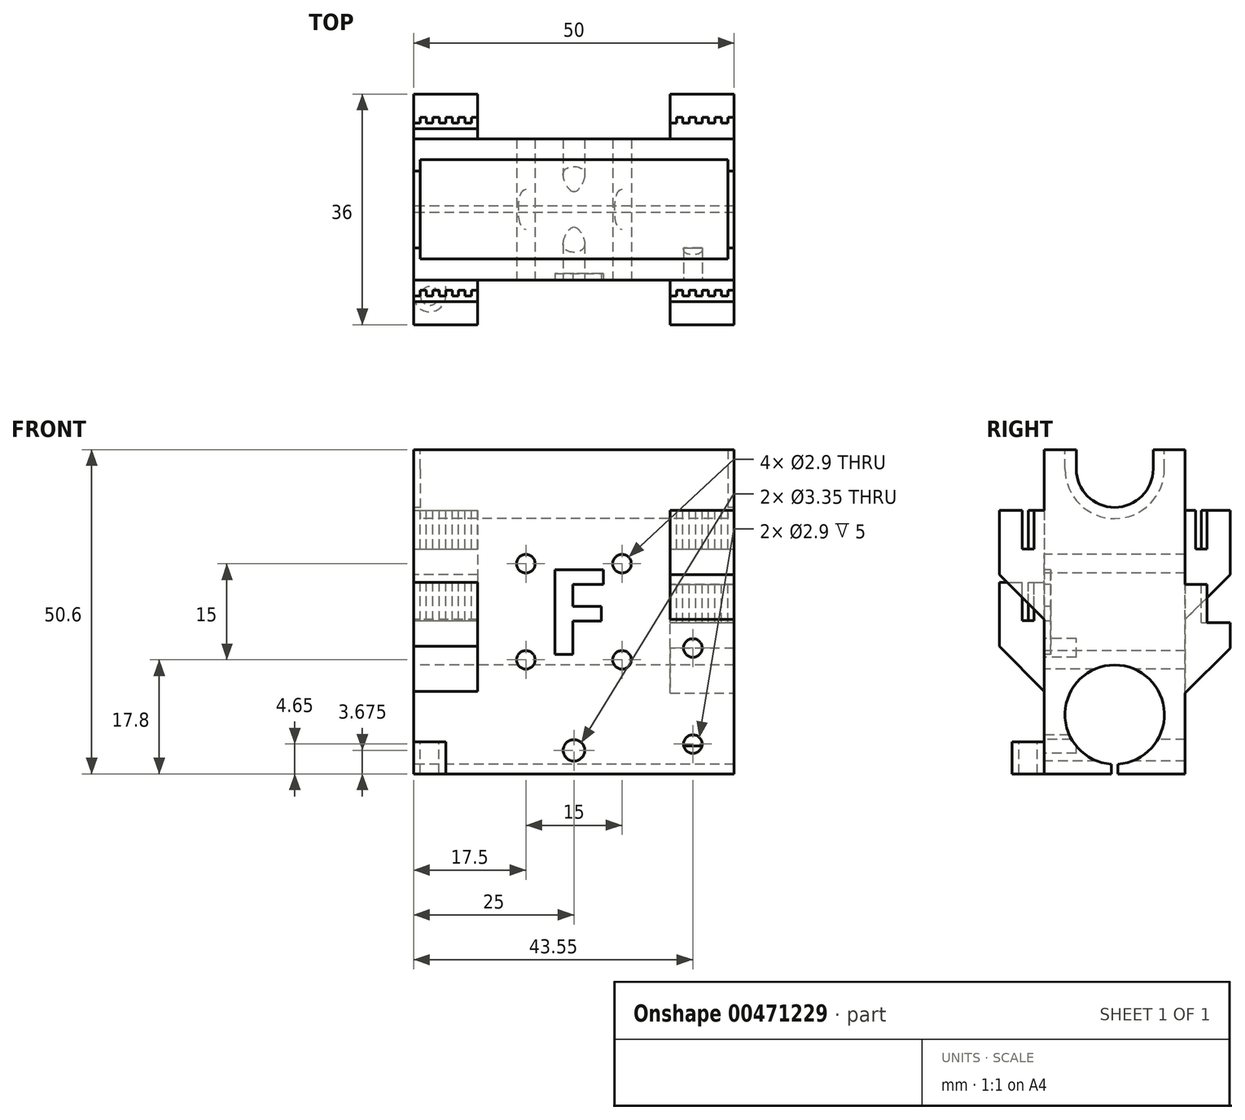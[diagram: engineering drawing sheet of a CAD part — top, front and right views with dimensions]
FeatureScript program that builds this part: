
annotation { "Feature Type Name" : "Feature", "Feature Type Description" : "" }
export const myFeature = defineFeature(function(context is Context, id is Id, definition is map)
    precondition{}
    {
        {
            assignVariable(context, id + "F0", {"name" : "LM8LUU", "anyValue" : 0});
        }
        {
            var Q0;
            Q0=qCreatedBy(makeId("Top.planeOp"),FACE);
            var sketch = newSketch(context, id + "F1", { "sketchPlane" : qUnion([Q0])});
            skLineSegment(sketch, "E0.bottom", {"start": v(0, 0) * mm, "end": v(50, 0) * mm});
            skLineSegment(sketch, "E0.top", {"start": v(0, 22) * mm, "end": v(50, 22) * mm});
            skLineSegment(sketch, "E0.left", {"start": v(0, 0) * mm, "end": v(0, 22) * mm});
            skLineSegment(sketch, "E0.right", {"start": v(50, 0) * mm, "end": v(50, 22) * mm});
            skSolve(sketch);
        }
        {
            var Q0;
            Q0=qSketchRegion(id+"F1",true);
            extrude(context, id + "F2", {"entities" : qUnion([Q0]), "depth" : 50.6 * mm});
        }
        {
            var Q0;
            Q0=makeQuery(id+"F2.opExtrude","SWEPT_FACE",FACE,{"disambiguationData":[OSD([sQuery(id+"F1.wireOp",EDGE,"E0.left")])]});
            var sketch = newSketch(context, id + "F3", { "sketchPlane" : qUnion([Q0])});
            skCircle(sketch, "E1", {"center": v(-11, 9.25) * mm, "radius": 7.75 * mm});
            skCircle(sketch, "E2", {"center": v(-11, 47.6) * mm, "radius": 6 * mm});
            skLineSegment(sketch, "E3", {"start": v(-22, 47.6) * mm, "end": v(0, 47.6) * mm, "construction": true});
            skLineSegment(sketch, "E4", {"start": v(-17, 50.6) * mm, "end": v(-17, 47.6) * mm});
            skLineSegment(sketch, "E5", {"start": v(-5, 50.6) * mm, "end": v(-5, 47.6) * mm});
            skLineSegment(sketch, "E6", {"start": v(-22, 9.25) * mm, "end": v(0, 9.25) * mm, "construction": true});
            skLineSegment(sketch, "E7", {"start": v(-11, 9.25) * mm, "end": v(-11, 0) * mm, "construction": true});
            skLineSegment(sketch, "E8", {"start": v(-11, 0) * mm, "end": v(-11.5, 0) * mm});
            skLineSegment(sketch, "E9", {"start": v(-11.5, 0) * mm, "end": v(-11.5, 1.52) * mm});
            skLineSegment(sketch, "E10", {"start": v(-11.5, 1.52) * mm, "end": v(-10.5, 1.52) * mm});
            skLineSegment(sketch, "E11", {"start": v(-10.5, 1.52) * mm, "end": v(-10.5, 0) * mm});
            skLineSegment(sketch, "E12", {"start": v(-10.5, 0) * mm, "end": v(-11, 0) * mm});
            skLineSegment(sketch, "E13", {"start": v(-11, 15.6) * mm, "end": v(-11, 17) * mm});
            skLineSegment(sketch, "E14", {"start": v(-11, 15.6) * mm, "end": v(-6.4, 15.5) * mm});
            skLineSegment(sketch, "E15", {"start": v(-11, 15.6) * mm, "end": v(-15.6, 15.5) * mm});
            skCircle(sketch, "E16", {"center": v(-11, 47.6) * mm, "radius": 7.75 * mm});
            skLineSegment(sketch, "E17", {"start": v(-3.25, 47.6) * mm, "end": v(-3.25, 50.6) * mm});
            skLineSegment(sketch, "E18", {"start": v(-18.75, 47.6) * mm, "end": v(-18.75, 50.6) * mm});
            skSolve(sketch);
        }
        {
            var Q0;
            {var subQ0=sQuery(id+"F3.wireOp",EDGE,"E14");var subQ1=sQuery(id+"F3.wireOp",EDGE,"E1");var subQ3=makeQuery(id+"F3.imprint","INTERSECT",VERTEX,{"disambiguationData":[OD(0.0)],"derivedFrom":[subQ1,subQ0]});Q0=makeQuery(id+"F3.imprint","IMPRINT",FACE,{"disambiguationData":[TD([[makeQuery(id+"F3.imprint","IMPRINT",EDGE,{"disambiguationData":[TD([[subQ3,-1.0]])],"derivedFrom":subQ1}),1.0]])]});}
            var Q1;
            {var subQ0=sQuery(id+"F3.wireOp",EDGE,"E15");var subQ1=sQuery(id+"F3.wireOp",EDGE,"E1");var subQ3=makeQuery(id+"F3.imprint","INTERSECT",VERTEX,{"disambiguationData":[OD(0.0)],"derivedFrom":[subQ1,subQ0]});Q1=makeQuery(id+"F3.imprint","IMPRINT",FACE,{"disambiguationData":[TD([[makeQuery(id+"F3.imprint","IMPRINT",EDGE,{"disambiguationData":[TD([[subQ3,1.0]])],"derivedFrom":subQ1}),1.0]])]});}
            var Q2;
            Q2=makeQuery(id+"F3.imprint","IMPRINT",FACE,{"disambiguationData":[TD([[makeQuery(id+"F3.imprint","IMPRINT",EDGE,{"derivedFrom":sQuery(id+"F3.wireOp",EDGE,"E8")}),-1.0]])]});
            var Q3;
            {var subQ0=sQuery(id+"F3.wireOp",EDGE,"E10");Q3=makeQuery(id+"F3.imprint","IMPRINT",FACE,{"disambiguationData":[TD([[makeQuery(id+"F3.imprint","IMPRINT",EDGE,{"derivedFrom":subQ0}),-1.0]])]});}
            var Q4;
            {var subQ3=sQuery(id+"F3.wireOp",EDGE,"E13");Q4=makeQuery(id+"F3.imprint","IMPRINT",FACE,{"disambiguationData":[TD([[makeQuery(id+"F3.imprint","IMPRINT",EDGE,{"derivedFrom":subQ3}),-1.0]])]});}
            var Q5;
            {var subQ3=sQuery(id+"F3.wireOp",EDGE,"E13");Q5=makeQuery(id+"F3.imprint","IMPRINT",FACE,{"disambiguationData":[TD([[makeQuery(id+"F3.imprint","IMPRINT",EDGE,{"derivedFrom":subQ3}),1.0]])]});}
            var Q6;
            {var subQ7=sQuery(id+"F3.wireOp",EDGE,"E10");Q6=makeQuery(id+"F3.imprint","IMPRINT",FACE,{"disambiguationData":[TD([[makeQuery(id+"F3.imprint","IMPRINT",EDGE,{"derivedFrom":subQ7}),1.0]])]});}
            var Q7;
            {var subQ3=sQuery(id+"F3.wireOp",EDGE,"E5");Q7=makeQuery(id+"F3.imprint","IMPRINT",FACE,{"disambiguationData":[TD([[makeQuery(id+"F3.imprint","IMPRINT",EDGE,{"derivedFrom":subQ3}),-1.0]])]});}
            var Q8;
            {var subQ0=sQuery(id+"F3.wireOp",EDGE,"E4");Q8=makeQuery(id+"F3.imprint","IMPRINT",FACE,{"disambiguationData":[TD([[makeQuery(id+"F3.imprint","IMPRINT",EDGE,{"derivedFrom":subQ0}),1.0]])]});}
            var Q9;
            {var subQ0=sQuery(id+"F3.wireOp",EDGE,"E4");Q9=makeQuery(id+"F3.imprint","IMPRINT",FACE,{"disambiguationData":[TD([[makeQuery(id+"F3.imprint","IMPRINT",EDGE,{"derivedFrom":subQ0}),1.0]])]});}
            var Q10;
            {var subQ3=sQuery(id+"F3.wireOp",EDGE,"E5");Q10=makeQuery(id+"F3.imprint","IMPRINT",FACE,{"disambiguationData":[TD([[makeQuery(id+"F3.imprint","IMPRINT",EDGE,{"derivedFrom":subQ3}),-1.0]])]});}
            var Q11;
            {var subQ1=sQuery(id+"F3.wireOp",EDGE,"E2");var subQ4=makeQuery(id+"F3.imprint","INTERSECT",VERTEX,{"derivedFrom":[subQ1,sQuery(id+"F3.wireOp",EDGE,"E5")]});Q11=makeQuery(id+"F3.imprint","IMPRINT",FACE,{"disambiguationData":[TD([[makeQuery(id+"F3.imprint","IMPRINT",EDGE,{"disambiguationData":[TD([[subQ4,-1.0]])],"derivedFrom":subQ1}),1.0]])]});}
            extrude(context, id + "F4", {"entities" : qUnion([Q0, Q1, Q2, Q3, Q4, Q5, Q6, Q7, Q8, Q9, Q10, Q11]), "operationType" : NewBodyOperationType.REMOVE, "endBound" : BoundingType.THROUGH_ALL, "oppositeDirection" : true, "depth" : 25 * mm});
        }
        {
            var Q0;
            {var subQ3=sQuery(id+"F3.wireOp",EDGE,"E4");Q0=makeQuery(id+"F3.imprint","IMPRINT",FACE,{"disambiguationData":[TD([[makeQuery(id+"F3.imprint","IMPRINT",EDGE,{"derivedFrom":subQ3}),-1.0]])]});}
            var Q1;
            {var subQ3=sQuery(id+"F3.wireOp",EDGE,"E18");Q1=makeQuery(id+"F3.imprint","IMPRINT",FACE,{"disambiguationData":[TD([[makeQuery(id+"F3.imprint","IMPRINT",EDGE,{"derivedFrom":subQ3}),-1.0]])]});}
            var Q2;
            {var subQ3=sQuery(id+"F3.wireOp",EDGE,"E17");Q2=makeQuery(id+"F3.imprint","IMPRINT",FACE,{"disambiguationData":[TD([[makeQuery(id+"F3.imprint","IMPRINT",EDGE,{"derivedFrom":subQ3}),1.0]])]});}
            extrude(context, id + "F5", {"entities" : qUnion([Q0, Q1, Q2]), "operationType" : NewBodyOperationType.REMOVE, "oppositeDirection" : true, "depth" : 49 * mm});
        }
        {
            var Q0;
            {var subQ3=sQuery(id+"F3.wireOp",EDGE,"E4");Q0=makeQuery(id+"F3.imprint","IMPRINT",FACE,{"disambiguationData":[TD([[makeQuery(id+"F3.imprint","IMPRINT",EDGE,{"derivedFrom":subQ3}),-1.0]])]});}
            var Q1;
            {var subQ3=sQuery(id+"F3.wireOp",EDGE,"E18");Q1=makeQuery(id+"F3.imprint","IMPRINT",FACE,{"disambiguationData":[TD([[makeQuery(id+"F3.imprint","IMPRINT",EDGE,{"derivedFrom":subQ3}),-1.0]])]});}
            var Q2;
            {var subQ3=sQuery(id+"F3.wireOp",EDGE,"E17");Q2=makeQuery(id+"F3.imprint","IMPRINT",FACE,{"disambiguationData":[TD([[makeQuery(id+"F3.imprint","IMPRINT",EDGE,{"derivedFrom":subQ3}),1.0]])]});}
            extrude(context, id + "F6", {"entities" : qUnion([Q0, Q1, Q2]), "operationType" : NewBodyOperationType.ADD, "oppositeDirection" : true, "depth" : (25 - getVariable(context, 'LM8LUU')) * mm});
        }
        {
            var Q0;
            {var subQ3=sQuery(id+"F3.wireOp",EDGE,"E4");Q0=makeQuery(id+"F3.imprint","IMPRINT",FACE,{"disambiguationData":[TD([[makeQuery(id+"F3.imprint","IMPRINT",EDGE,{"derivedFrom":subQ3}),-1.0]])]});}
            var Q1;
            {var subQ3=sQuery(id+"F3.wireOp",EDGE,"E18");Q1=makeQuery(id+"F3.imprint","IMPRINT",FACE,{"disambiguationData":[TD([[makeQuery(id+"F3.imprint","IMPRINT",EDGE,{"derivedFrom":subQ3}),-1.0]])]});}
            var Q2;
            {var subQ3=sQuery(id+"F3.wireOp",EDGE,"E17");Q2=makeQuery(id+"F3.imprint","IMPRINT",FACE,{"disambiguationData":[TD([[makeQuery(id+"F3.imprint","IMPRINT",EDGE,{"derivedFrom":subQ3}),1.0]])]});}
            extrude(context, id + "F7", {"entities" : qUnion([Q0, Q1, Q2]), "operationType" : NewBodyOperationType.REMOVE, "oppositeDirection" : true, "depth" : (25 + getVariable(context, 'LM8LUU')) * mm});
        }
        {
            var Q0;
            {var subQ3=sQuery(id+"F3.wireOp",EDGE,"E4");Q0=makeQuery(id+"F3.imprint","IMPRINT",FACE,{"disambiguationData":[TD([[makeQuery(id+"F3.imprint","IMPRINT",EDGE,{"derivedFrom":subQ3}),-1.0]])]});}
            var Q1;
            {var subQ3=sQuery(id+"F3.wireOp",EDGE,"E18");Q1=makeQuery(id+"F3.imprint","IMPRINT",FACE,{"disambiguationData":[TD([[makeQuery(id+"F3.imprint","IMPRINT",EDGE,{"derivedFrom":subQ3}),-1.0]])]});}
            var Q2;
            {var subQ3=sQuery(id+"F3.wireOp",EDGE,"E17");Q2=makeQuery(id+"F3.imprint","IMPRINT",FACE,{"disambiguationData":[TD([[makeQuery(id+"F3.imprint","IMPRINT",EDGE,{"derivedFrom":subQ3}),1.0]])]});}
            extrude(context, id + "F8", {"entities" : qUnion([Q0, Q1, Q2]), "operationType" : NewBodyOperationType.ADD, "oppositeDirection" : true, "depth" : 1 * mm});
        }
        {
            var Q0;
            Q0=makeQuery(id+"F2.opExtrude","SWEPT_FACE",FACE,{"disambiguationData":[OSD([sQuery(id+"F1.wireOp",EDGE,"E0.bottom")])]});
            var sketch = newSketch(context, id + "F9", { "sketchPlane" : qUnion([Q0])});
            skLineSegment(sketch, "E19.bottom", {"start": v(0, 29.9) * mm, "end": v(10, 29.9) * mm});
            skLineSegment(sketch, "E19.top", {"start": v(0, 9.9) * mm, "end": v(10, 9.9) * mm});
            skLineSegment(sketch, "E19.left", {"start": v(0, 29.9) * mm, "end": v(0, 9.9) * mm});
            skLineSegment(sketch, "E19.right", {"start": v(10, 29.9) * mm, "end": v(10, 9.9) * mm});
            skLineSegment(sketch, "E20.bottom", {"start": v(50, 41.1) * mm, "end": v(40, 41.1) * mm});
            skLineSegment(sketch, "E20.top", {"start": v(50, 21.1) * mm, "end": v(40, 21.1) * mm});
            skLineSegment(sketch, "E20.left", {"start": v(50, 41.1) * mm, "end": v(50, 21.1) * mm});
            skLineSegment(sketch, "E20.right", {"start": v(40, 41.1) * mm, "end": v(40, 21.1) * mm});
            skPoint(sketch, "E21", {"position": v(0, 47.6) * mm});
            skPoint(sketch, "E22", {"position": v(0, 9.4) * mm});
            skSolve(sketch);
        }
        {
            var Q0;
            Q0=qSketchRegion(id+"F9",true);
            extrude(context, id + "F10", {"entities" : qUnion([Q0]), "operationType" : NewBodyOperationType.ADD, "depth" : 7 * mm});
        }
        {
            var Q0;
            Q0=makeQuery(id+"F10.opExtrude","CAP_EDGE",EDGE,{"disambiguationData":[OSD([sQuery(id+"F9.wireOp",EDGE,"E19.top")])],"isStart":false});
            var Q1;
            Q1=makeQuery(id+"F10.opExtrude","CAP_EDGE",EDGE,{"disambiguationData":[OSD([sQuery(id+"F9.wireOp",EDGE,"E20.top")])],"isStart":false});
            chamfer(context, id + "F11", {"entities" : qUnion([Q0, Q1]), "width" : 10 * mm, "tangentPropagation" : true});
        }
        {
            var Q0;
            Q0=makeQuery(id+"F10.opExtrude","SWEPT_FACE",FACE,{"disambiguationData":[OSD([sQuery(id+"F9.wireOp",EDGE,"E19.bottom")])]});
            var sketch = newSketch(context, id + "F12", { "sketchPlane" : qUnion([Q0])});
            skLineSegment(sketch, "E23", {"start": v(-935.9, 0) * mm, "end": v(-935.88, -4.54) * mm});
            skLineSegment(sketch, "E24.left", {"start": v(0, -3.4) * mm, "end": v(0, -1.6) * mm});
            skLineSegment(sketch, "E25", {"start": v(6, -2.5) * mm, "end": v(7, -2.5) * mm});
            skLineSegment(sketch, "E26", {"start": v(4, -2.5) * mm, "end": v(5, -2.5) * mm});
            skLineSegment(sketch, "E27", {"start": v(0, -2.5) * mm, "end": v(1, -2.5) * mm});
            skLineSegment(sketch, "E28", {"start": v(7, -1.6) * mm, "end": v(8, -1.6) * mm});
            skLineSegment(sketch, "E29", {"start": v(2, -2.5) * mm, "end": v(3, -2.5) * mm});
            skLineSegment(sketch, "E30", {"start": v(3, -1.6) * mm, "end": v(4, -1.6) * mm});
            skLineSegment(sketch, "E31", {"start": v(8, -2.5) * mm, "end": v(9, -2.5) * mm});
            skLineSegment(sketch, "E32", {"start": v(8, -1.6) * mm, "end": v(8, -2.5) * mm});
            skLineSegment(sketch, "E33", {"start": v(9, -2.5) * mm, "end": v(9, -1.6) * mm});
            skLineSegment(sketch, "E34", {"start": v(10, -1.6) * mm, "end": v(10, -2.5) * mm});
            skLineSegment(sketch, "E35", {"start": v(6, -1.6) * mm, "end": v(6, -2.5) * mm});
            skLineSegment(sketch, "E36", {"start": v(2, -1.6) * mm, "end": v(2, -2.5) * mm});
            skLineSegment(sketch, "E37", {"start": v(1, -1.6) * mm, "end": v(2, -1.6) * mm});
            skLineSegment(sketch, "E38", {"start": v(1, -2.5) * mm, "end": v(1, -1.6) * mm});
            skLineSegment(sketch, "E39", {"start": v(9, -1.6) * mm, "end": v(10, -1.6) * mm});
            skLineSegment(sketch, "E40", {"start": v(5, -1.6) * mm, "end": v(6, -1.6) * mm});
            skLineSegment(sketch, "E41", {"start": v(5, -2.5) * mm, "end": v(5, -1.6) * mm});
            skLineSegment(sketch, "E42", {"start": v(3, -2.5) * mm, "end": v(3, -1.6) * mm});
            skLineSegment(sketch, "E43", {"start": v(4, -1.6) * mm, "end": v(4, -2.5) * mm});
            skLineSegment(sketch, "E44", {"start": v(7, -2.5) * mm, "end": v(7, -1.6) * mm});
            skLineSegment(sketch, "E45", {"start": v(0, -1.6) * mm, "end": v(0, -2.5) * mm});
            skLineSegment(sketch, "E46", {"start": v(10, -2.5) * mm, "end": v(10, -3.4) * mm});
            skLineSegment(sketch, "E47", {"start": v(0, -3.4) * mm, "end": v(10, -3.4) * mm});
            skLineSegment(sketch, "E48", {"start": v(5.3, -1.6) * mm, "end": v(5.3, 0) * mm});
            skSolve(sketch);
        }
        {
            var Q0;
            Q0=qSketchRegion(id+"F12",true);
            extrude(context, id + "F13", {"entities" : qUnion([Q0]), "operationType" : NewBodyOperationType.REMOVE, "oppositeDirection" : true, "depth" : 6 * mm});
        }
        {
            var Q0;
            Q0=makeQuery(id+"F10.opExtrude","SWEPT_FACE",FACE,{"disambiguationData":[OSD([sQuery(id+"F9.wireOp",EDGE,"E20.bottom")])]});
            var sketch = newSketch(context, id + "F14", { "sketchPlane" : qUnion([Q0])});
            skLineSegment(sketch, "E49.left", {"start": v(40, -3.4) * mm, "end": v(40, -1.6) * mm});
            skLineSegment(sketch, "E50", {"start": v(46, -2.5) * mm, "end": v(47, -2.5) * mm});
            skLineSegment(sketch, "E51", {"start": v(44, -2.5) * mm, "end": v(45, -2.5) * mm});
            skLineSegment(sketch, "E52", {"start": v(40, -2.5) * mm, "end": v(41, -2.5) * mm});
            skLineSegment(sketch, "E53", {"start": v(47, -1.6) * mm, "end": v(48, -1.6) * mm});
            skLineSegment(sketch, "E54", {"start": v(42, -2.5) * mm, "end": v(43, -2.5) * mm});
            skLineSegment(sketch, "E55", {"start": v(43, -1.6) * mm, "end": v(44, -1.6) * mm});
            skLineSegment(sketch, "E56", {"start": v(48, -2.5) * mm, "end": v(49, -2.5) * mm});
            skLineSegment(sketch, "E57", {"start": v(48, -1.6) * mm, "end": v(48, -2.5) * mm});
            skLineSegment(sketch, "E58", {"start": v(49, -2.5) * mm, "end": v(49, -1.6) * mm});
            skLineSegment(sketch, "E59", {"start": v(50, -1.6) * mm, "end": v(50, -2.5) * mm});
            skLineSegment(sketch, "E60", {"start": v(46, -1.6) * mm, "end": v(46, -2.5) * mm});
            skLineSegment(sketch, "E61", {"start": v(42, -1.6) * mm, "end": v(42, -2.5) * mm});
            skLineSegment(sketch, "E62", {"start": v(41, -1.6) * mm, "end": v(42, -1.6) * mm});
            skLineSegment(sketch, "E63", {"start": v(41, -2.5) * mm, "end": v(41, -1.6) * mm});
            skLineSegment(sketch, "E64", {"start": v(49, -1.6) * mm, "end": v(50, -1.6) * mm});
            skLineSegment(sketch, "E65", {"start": v(45, -1.6) * mm, "end": v(46, -1.6) * mm});
            skLineSegment(sketch, "E66", {"start": v(45, -2.5) * mm, "end": v(45, -1.6) * mm});
            skLineSegment(sketch, "E67", {"start": v(43, -2.5) * mm, "end": v(43, -1.6) * mm});
            skLineSegment(sketch, "E68", {"start": v(44, -1.6) * mm, "end": v(44, -2.5) * mm});
            skLineSegment(sketch, "E69", {"start": v(47, -2.5) * mm, "end": v(47, -1.6) * mm});
            skLineSegment(sketch, "E70", {"start": v(40, -1.6) * mm, "end": v(40, -2.5) * mm});
            skLineSegment(sketch, "E71", {"start": v(50, -2.5) * mm, "end": v(50, -3.4) * mm});
            skLineSegment(sketch, "E72", {"start": v(40, -3.4) * mm, "end": v(50, -3.4) * mm});
            skLineSegment(sketch, "E73", {"start": v(45.23, -1.6) * mm, "end": v(45.23, 0) * mm});
            skSolve(sketch);
        }
        {
            var Q0;
            Q0=qSketchRegion(id+"F14",true);
            extrude(context, id + "F15", {"entities" : qUnion([Q0]), "operationType" : NewBodyOperationType.REMOVE, "oppositeDirection" : true, "depth" : 6 * mm});
        }
        {
            var Q0;
            Q0=makeQuery(id+"F2.opExtrude","SWEPT_FACE",FACE,{"disambiguationData":[OSD([sQuery(id+"F1.wireOp",EDGE,"E0.top")])]});
            var sketch = newSketch(context, id + "F16", { "sketchPlane" : qUnion([Q0])});
            skLineSegment(sketch, "E74.bottom", {"start": v(-50, 9.6) * mm, "end": v(-40, 9.6) * mm});
            skLineSegment(sketch, "E74.top", {"start": v(-50, 29.6) * mm, "end": v(-40, 29.6) * mm});
            skLineSegment(sketch, "E74.left", {"start": v(-50, 9.6) * mm, "end": v(-50, 29.6) * mm});
            skLineSegment(sketch, "E74.right", {"start": v(-40, 9.6) * mm, "end": v(-40, 29.6) * mm});
            skLineSegment(sketch, "E75.bottom", {"start": v(0, 41.1) * mm, "end": v(-10, 41.1) * mm});
            skLineSegment(sketch, "E75.top", {"start": v(0, 21.1) * mm, "end": v(-10, 21.1) * mm});
            skLineSegment(sketch, "E75.left", {"start": v(0, 41.1) * mm, "end": v(0, 21.1) * mm});
            skLineSegment(sketch, "E75.right", {"start": v(-10, 41.1) * mm, "end": v(-10, 21.1) * mm});
            skSolve(sketch);
        }
        {
            var Q0;
            Q0=qSketchRegion(id+"F16",true);
            extrude(context, id + "F17", {"entities" : qUnion([Q0]), "operationType" : NewBodyOperationType.ADD, "depth" : 7 * mm});
        }
        {
            var Q0;
            Q0=makeQuery(id+"F17.opExtrude","SWEPT_FACE",FACE,{"disambiguationData":[OSD([sQuery(id+"F16.wireOp",EDGE,"E74.top")])]});
            var sketch = newSketch(context, id + "F18", { "sketchPlane" : qUnion([Q0])});
            skLineSegment(sketch, "E76.left", {"start": v(40, 23.6) * mm, "end": v(40, 25.4) * mm});
            skLineSegment(sketch, "E77", {"start": v(46, 24.5) * mm, "end": v(47, 24.5) * mm});
            skLineSegment(sketch, "E78", {"start": v(44, 24.5) * mm, "end": v(45, 24.5) * mm});
            skLineSegment(sketch, "E79", {"start": v(40, 24.5) * mm, "end": v(41, 24.5) * mm});
            skLineSegment(sketch, "E80", {"start": v(47, 25.4) * mm, "end": v(48, 25.4) * mm});
            skLineSegment(sketch, "E81", {"start": v(42, 24.5) * mm, "end": v(43, 24.5) * mm});
            skLineSegment(sketch, "E82", {"start": v(43, 25.4) * mm, "end": v(44, 25.4) * mm});
            skLineSegment(sketch, "E83", {"start": v(48, 24.5) * mm, "end": v(49, 24.5) * mm});
            skLineSegment(sketch, "E84", {"start": v(48, 25.4) * mm, "end": v(48, 24.5) * mm});
            skLineSegment(sketch, "E85", {"start": v(49, 24.5) * mm, "end": v(49, 25.4) * mm});
            skLineSegment(sketch, "E86", {"start": v(50, 25.4) * mm, "end": v(50, 24.5) * mm});
            skLineSegment(sketch, "E87", {"start": v(46, 25.4) * mm, "end": v(46, 24.5) * mm});
            skLineSegment(sketch, "E88", {"start": v(42, 25.4) * mm, "end": v(42, 24.5) * mm});
            skLineSegment(sketch, "E89", {"start": v(41, 25.4) * mm, "end": v(42, 25.4) * mm});
            skLineSegment(sketch, "E90", {"start": v(41, 24.5) * mm, "end": v(41, 25.4) * mm});
            skLineSegment(sketch, "E91", {"start": v(49, 25.4) * mm, "end": v(50, 25.4) * mm});
            skLineSegment(sketch, "E92", {"start": v(45, 25.4) * mm, "end": v(46, 25.4) * mm});
            skLineSegment(sketch, "E93", {"start": v(45, 24.5) * mm, "end": v(45, 25.4) * mm});
            skLineSegment(sketch, "E94", {"start": v(43, 24.5) * mm, "end": v(43, 25.4) * mm});
            skLineSegment(sketch, "E95", {"start": v(44, 25.4) * mm, "end": v(44, 24.5) * mm});
            skLineSegment(sketch, "E96", {"start": v(47, 24.5) * mm, "end": v(47, 25.4) * mm});
            skLineSegment(sketch, "E97", {"start": v(40, 25.4) * mm, "end": v(40, 24.5) * mm});
            skLineSegment(sketch, "E98", {"start": v(50, 24.5) * mm, "end": v(50, 23.6) * mm});
            skLineSegment(sketch, "E99", {"start": v(40, 23.6) * mm, "end": v(50, 23.6) * mm});
            skLineSegment(sketch, "E100", {"start": v(45, 23.6) * mm, "end": v(45, 22) * mm});
            skSolve(sketch);
        }
        {
            var Q0;
            {var subQ4=sQuery(id+"F18.wireOp",EDGE,"E76.left");Q0=makeQuery(id+"F18.imprint","IMPRINT",FACE,{"disambiguationData":[TD([[makeQuery(id+"F18.imprint","IMPRINT",EDGE,{"derivedFrom":subQ4}),1.0]])]});}
            extrude(context, id + "F19", {"entities" : qUnion([Q0]), "operationType" : NewBodyOperationType.REMOVE, "oppositeDirection" : true, "depth" : 6 * mm});
        }
        {
            var Q0;
            Q0=makeQuery(id+"F17.opExtrude","SWEPT_FACE",FACE,{"disambiguationData":[OSD([sQuery(id+"F16.wireOp",EDGE,"E75.bottom")])]});
            var sketch = newSketch(context, id + "F20", { "sketchPlane" : qUnion([Q0])});
            skLineSegment(sketch, "E101", {"start": v(6, 24.5) * mm, "end": v(7, 24.5) * mm});
            skLineSegment(sketch, "E102", {"start": v(4, 24.5) * mm, "end": v(5, 24.5) * mm});
            skLineSegment(sketch, "E103", {"start": v(0, 24.5) * mm, "end": v(1, 24.5) * mm});
            skLineSegment(sketch, "E104", {"start": v(7, 25.4) * mm, "end": v(8, 25.4) * mm});
            skLineSegment(sketch, "E105", {"start": v(2, 24.5) * mm, "end": v(3, 24.5) * mm});
            skLineSegment(sketch, "E106", {"start": v(3, 25.4) * mm, "end": v(4, 25.4) * mm});
            skLineSegment(sketch, "E107", {"start": v(8, 24.5) * mm, "end": v(9, 24.5) * mm});
            skLineSegment(sketch, "E108", {"start": v(8, 25.4) * mm, "end": v(8, 24.5) * mm});
            skLineSegment(sketch, "E109", {"start": v(9, 24.5) * mm, "end": v(9, 25.4) * mm});
            skLineSegment(sketch, "E110", {"start": v(10, 25.4) * mm, "end": v(10, 24.5) * mm});
            skLineSegment(sketch, "E111", {"start": v(6, 25.4) * mm, "end": v(6, 24.5) * mm});
            skLineSegment(sketch, "E112", {"start": v(2, 25.4) * mm, "end": v(2, 24.5) * mm});
            skLineSegment(sketch, "E113", {"start": v(1, 25.4) * mm, "end": v(2, 25.4) * mm});
            skLineSegment(sketch, "E114", {"start": v(1, 24.5) * mm, "end": v(1, 25.4) * mm});
            skLineSegment(sketch, "E115", {"start": v(9, 25.4) * mm, "end": v(10, 25.4) * mm});
            skLineSegment(sketch, "E116", {"start": v(5, 25.4) * mm, "end": v(6, 25.4) * mm});
            skLineSegment(sketch, "E117", {"start": v(5, 24.5) * mm, "end": v(5, 25.4) * mm});
            skLineSegment(sketch, "E118", {"start": v(3, 24.5) * mm, "end": v(3, 25.4) * mm});
            skLineSegment(sketch, "E119", {"start": v(4, 25.4) * mm, "end": v(4, 24.5) * mm});
            skLineSegment(sketch, "E120", {"start": v(7, 24.5) * mm, "end": v(7, 25.4) * mm});
            skLineSegment(sketch, "E121", {"start": v(10, 24.5) * mm, "end": v(10, 23.6) * mm});
            skLineSegment(sketch, "E122", {"start": v(0, 23.6) * mm, "end": v(10, 23.6) * mm});
            skLineSegment(sketch, "E123", {"start": v(5, 23.6) * mm, "end": v(5, 22) * mm});
            skLineSegment(sketch, "E124", {"start": v(0, 23.6) * mm, "end": v(0, 24.5) * mm});
            skSolve(sketch);
        }
        {
            var Q0;
            Q0=makeQuery(id+"F20.imprint","IMPRINT",FACE,{"disambiguationData":[TD([[makeQuery(id+"F20.imprint","IMPRINT",EDGE,{"derivedFrom":sQuery(id+"F20.wireOp",EDGE,"E101")}),-1.0]])]});
            extrude(context, id + "F21", {"entities" : qUnion([Q0]), "operationType" : NewBodyOperationType.REMOVE, "oppositeDirection" : true, "depth" : 6 * mm});
        }
        {
            var Q0;
            Q0=makeQuery(id+"F17.opExtrude","CAP_EDGE",EDGE,{"disambiguationData":[OSD([sQuery(id+"F16.wireOp",EDGE,"E75.top")])],"isStart":false});
            var Q1;
            Q1=makeQuery(id+"F17.opExtrude","CAP_EDGE",EDGE,{"disambiguationData":[OSD([sQuery(id+"F16.wireOp",EDGE,"E74.bottom")])],"isStart":false});
            chamfer(context, id + "F22", {"entities" : qUnion([Q0, Q1]), "width" : 10 * mm, "tangentPropagation" : true});
        }
        {
            var Q0;
            Q0=makeQuery(id+"F2.opExtrude","SWEPT_FACE",FACE,{"disambiguationData":[OSD([sQuery(id+"F1.wireOp",EDGE,"E0.bottom")])]});
            var sketch = newSketch(context, id + "F23", { "sketchPlane" : qUnion([Q0])});
            skCircle(sketch, "E125", {"center": v(17.5, 32.8) * mm, "radius": 1.45 * mm});
            skCircle(sketch, "E126", {"center": v(32.5, 32.8) * mm, "radius": 1.45 * mm});
            skCircle(sketch, "E127", {"center": v(17.5, 17.8) * mm, "radius": 1.45 * mm});
            skCircle(sketch, "E128", {"center": v(32.5, 17.8) * mm, "radius": 1.45 * mm});
            skLineSegment(sketch, "E129", {"start": v(17.5, 32.8) * mm, "end": v(0, 32.8) * mm});
            skLineSegment(sketch, "E130", {"start": v(32.5, 17.8) * mm, "end": v(50, 17.8) * mm});
            skLineSegment(sketch, "E131", {"start": v(32.5, 32.8) * mm, "end": v(32.5, 50.6) * mm});
            skLineSegment(sketch, "E132", {"start": v(17.5, 17.8) * mm, "end": v(17.5, 0) * mm});
            skCircle(sketch, "E133", {"center": v(25, 3.68) * mm, "radius": 1.68 * mm});
            skLineSegment(sketch, "E134", {"start": v(25, 0) * mm, "end": v(25, 13.82) * mm, "construction": true});
            skSolve(sketch);
        }
        {
            var Q0;
            Q0=qSketchRegion(id+"F23",true);
            var Q1;
            Q1=makeQuery(id+"F23.imprint","IMPRINT",FACE,{"disambiguationData":[TD([[makeQuery(id+"F23.imprint","IMPRINT",EDGE,{"derivedFrom":sQuery(id+"F23.wireOp",EDGE,"E125")}),1.0]])]});
            var Q2;
            Q2=makeQuery(id+"F23.imprint","IMPRINT",FACE,{"disambiguationData":[TD([[makeQuery(id+"F23.imprint","IMPRINT",EDGE,{"derivedFrom":sQuery(id+"F23.wireOp",EDGE,"E126")}),1.0]])]});
            var Q3;
            Q3=makeQuery(id+"F23.imprint","IMPRINT",FACE,{"disambiguationData":[TD([[makeQuery(id+"F23.imprint","IMPRINT",EDGE,{"derivedFrom":sQuery(id+"F23.wireOp",EDGE,"E128")}),1.0]])]});
            var Q4;
            Q4=makeQuery(id+"F23.imprint","IMPRINT",FACE,{"disambiguationData":[TD([[makeQuery(id+"F23.imprint","IMPRINT",EDGE,{"derivedFrom":sQuery(id+"F23.wireOp",EDGE,"E127")}),1.0]])]});
            extrude(context, id + "F24", {"entities" : qUnion([Q0, Q1, Q2, Q3, Q4]), "operationType" : NewBodyOperationType.REMOVE, "endBound" : BoundingType.THROUGH_ALL, "oppositeDirection" : true, "depth" : 25 * mm});
        }
        {
            var Q0;
            Q0=makeQuery(id+"F2.opExtrude","SWEPT_FACE",FACE,{"disambiguationData":[OSD([sQuery(id+"F1.wireOp",EDGE,"E0.bottom")])]});
            var sketch = newSketch(context, id + "F25", { "sketchPlane" : qUnion([Q0])});
            skCircle(sketch, "E135", {"center": v(43.55, 19.65) * mm, "radius": 1.45 * mm});
            skCircle(sketch, "E136", {"center": v(43.55, 4.65) * mm, "radius": 1.45 * mm});
            skSolve(sketch);
        }
        {
            var Q0;
            Q0=qSketchRegion(id+"F25",true);
            extrude(context, id + "F26", {"entities" : qUnion([Q0]), "operationType" : NewBodyOperationType.REMOVE, "oppositeDirection" : true, "depth" : 5 * mm});
        }
        {
            var Q0;
            Q0=makeQuery(id+"F2.opExtrude","SWEPT_FACE",FACE,{"disambiguationData":[OSD([sQuery(id+"F1.wireOp",EDGE,"E0.bottom")])]});
            var sketch = newSketch(context, id + "F27", { "sketchPlane" : qUnion([Q0])});
            skText(sketch, "E137", { "text": "F", "fontName": "OpenSans-Bold.ttf"});
            skLineSegment(sketch, "E138", {"start": v(17.5, 32.8) * mm, "end": v(17.5, 17.8) * mm, "construction": true});
            skLineSegment(sketch, "E139", {"start": v(17.5, 17.8) * mm, "end": v(32.5, 17.8) * mm, "construction": true});
            skLineSegment(sketch, "E140", {"start": v(32.5, 17.8) * mm, "end": v(32.5, 32.8) * mm, "construction": true});
            skLineSegment(sketch, "E141", {"start": v(32.5, 32.8) * mm, "end": v(17.5, 32.8) * mm, "construction": true});
            skLineSegment(sketch, "E142", {"start": v(17.5, 25.3) * mm, "end": v(20.4, 25.3) * mm, "construction": true});
            skLineSegment(sketch, "E143", {"start": v(29.6, 25.3) * mm, "end": v(32.5, 25.3) * mm, "construction": true});
            skLineSegment(sketch, "E144", {"start": v(25, 18.66) * mm, "end": v(25, 17.8) * mm, "construction": true});
            skLineSegment(sketch, "E145", {"start": v(25, 32.8) * mm, "end": v(25, 31.94) * mm, "construction": true});
            const initialGuessF27  = {"E137": [0.0204, 0.01866, 1, 0, 0.01328]};
            skSetInitialGuess(sketch, initialGuessF27);
            skSolve(sketch);
        }
        {
            var Q0;
            Q0=qSketchRegion(id+"F27",true);
            extrude(context, id + "F28", {"entities" : qUnion([Q0]), "operationType" : NewBodyOperationType.REMOVE, "oppositeDirection" : true, "depth" : 1 * mm});
        }
        {
            var Q0;
            Q0=makeQuery(id+"F2.opExtrude","SWEPT_FACE",FACE,{"disambiguationData":[OSD([sQuery(id+"F1.wireOp",EDGE,"E0.bottom")])]});
            var sketch = newSketch(context, id + "F29", { "sketchPlane" : qUnion([Q0])});
            skLineSegment(sketch, "E146.bottom", {"start": v(0, 0) * mm, "end": v(5, 0) * mm});
            skLineSegment(sketch, "E146.top", {"start": v(0, 5) * mm, "end": v(5, 5) * mm});
            skLineSegment(sketch, "E146.left", {"start": v(0, 0) * mm, "end": v(0, 5) * mm});
            skLineSegment(sketch, "E146.right", {"start": v(5, 0) * mm, "end": v(5, 5) * mm});
            skSolve(sketch);
        }
        {
            var Q0;
            Q0=qSketchRegion(id+"F29",true);
            extrude(context, id + "F30", {"entities" : qUnion([Q0]), "operationType" : NewBodyOperationType.ADD, "depth" : 5 * mm});
        }
        {
            var Q0;
            Q0=makeQuery(id+"F30.opExtrude","SWEPT_FACE",FACE,{"disambiguationData":[OSD([sQuery(id+"F29.wireOp",EDGE,"E146.top")])]});
            var sketch = newSketch(context, id + "F31", { "sketchPlane" : qUnion([Q0])});
            skCircle(sketch, "E147", {"center": v(2.5, -2.5) * mm, "radius": 1.45 * mm});
            skLineSegment(sketch, "E148", {"start": v(0, -2.5) * mm, "end": v(5, -2.5) * mm});
            skSolve(sketch);
        }
        {
            var Q0;
            Q0=qSketchRegion(id+"F31",true);
            extrude(context, id + "F32", {"entities" : qUnion([Q0]), "operationType" : NewBodyOperationType.REMOVE, "oppositeDirection" : true, "depth" : 25 * mm});
        }
        {
            var Q0;
            Q0=makeQuery(id+"F30.opExtrude","CAP_EDGE",EDGE,{"disambiguationData":[OSD([sQuery(id+"F29.wireOp",EDGE,"E146.left")])],"isStart":false});
            var Q1;
            Q1=makeQuery(id+"F30.opExtrude","CAP_EDGE",EDGE,{"disambiguationData":[OSD([sQuery(id+"F29.wireOp",EDGE,"E146.right")])],"isStart":false});
            fillet(context, id + "F33", {"entities" : qUnion([Q0, Q1]), "radius" : 2.5 * mm, "tangentPropagation" : true, "allowEdgeOverflow" : false});
        }
    });
